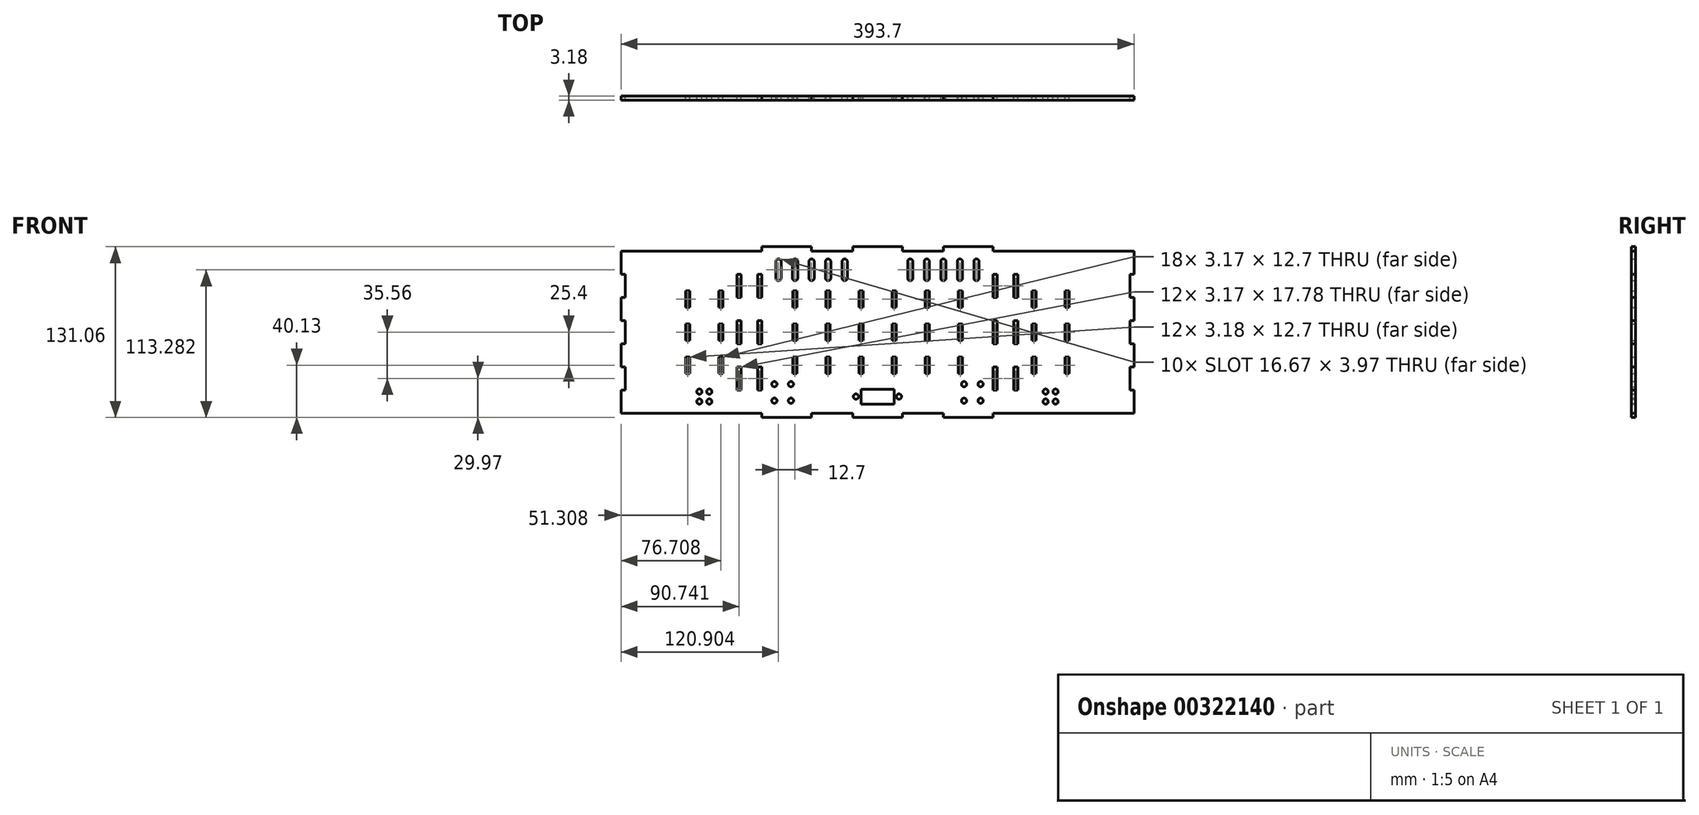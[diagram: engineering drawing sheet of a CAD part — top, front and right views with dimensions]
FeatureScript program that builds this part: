
annotation { "Feature Type Name" : "Feature", "Feature Type Description" : "" }
export const myFeature = defineFeature(function(context is Context, id is Id, definition is map)
    precondition{}
    {
        {
            var Q0;
            Q0=qCreatedBy(makeId("Front.planeOp"),FACE);
            var sketch = newSketch(context, id + "F0", { "sketchPlane" : qUnion([Q0])});
            skLineSegment(sketch, "E0.MirrorCS", {"start": v(-50.55, -65.53) * mm, "end": v(-50.55, -62.23) * mm});
            skLineSegment(sketch, "E1.MirrorCS", {"start": v(19.05, -65.53) * mm, "end": v(19.05, -62.23) * mm});
            skLineSegment(sketch, "E2.MirrorCS", {"start": v(50.55, -65.53) * mm, "end": v(50.55, -62.23) * mm});
            skLineSegment(sketch, "E3.MirrorCS", {"start": v(88.65, -65.53) * mm, "end": v(88.65, -62.23) * mm});
            skLineSegment(sketch, "E4.MirrorCS", {"start": v(-19.05, -65.53) * mm, "end": v(-19.05, -62.23) * mm});
            skLineSegment(sketch, "E5.MirrorCS", {"start": v(88.65, -65.53) * mm, "end": v(50.55, -65.53) * mm});
            skLineSegment(sketch, "E6.MirrorCS", {"start": v(-19.05, -65.53) * mm, "end": v(19.05, -65.53) * mm});
            skLineSegment(sketch, "E7.MirrorCS", {"start": v(-50.55, -65.53) * mm, "end": v(-19.05, -65.53) * mm, "construction": true});
            skLineSegment(sketch, "E8.MirrorCS", {"start": v(-88.65, -65.53) * mm, "end": v(-50.55, -65.53) * mm});
            skLineSegment(sketch, "E9.MirrorCS", {"start": v(-88.65, -65.53) * mm, "end": v(-88.65, -62.23) * mm});
            skLineSegment(sketch, "E10", {"start": v(-107.7, -62.23) * mm, "end": v(-88.65, -62.23) * mm});
            skLineSegment(sketch, "E11.trimOffspring", {"start": v(88.65, -62.23) * mm, "end": v(120.14, -62.23) * mm});
            skLineSegment(sketch, "E12.trimOffspring", {"start": v(19.05, -62.23) * mm, "end": v(50.55, -62.23) * mm});
            skLineSegment(sketch, "E13.trimOffspring", {"start": v(-50.55, -62.23) * mm, "end": v(-19.05, -62.23) * mm});
            skLineSegment(sketch, "E14", {"start": v(-107.7, 62.23) * mm, "end": v(-107.7, 44.45) * mm, "construction": true});
            skLineSegment(sketch, "E15.MirrorCS", {"start": v(-104.52, 26.67) * mm, "end": v(-104.52, 8.89) * mm, "construction": true});
            skLineSegment(sketch, "E16.MirrorCS", {"start": v(-107.7, -26.67) * mm, "end": v(-107.7, -8.89) * mm, "construction": true});
            skLineSegment(sketch, "E17.MirrorCS", {"start": v(-104.52, 44.45) * mm, "end": v(-104.52, 26.67) * mm});
            skLineSegment(sketch, "E18.MirrorCS", {"start": v(-104.52, -8.9) * mm, "end": v(-104.52, -26.67) * mm, "construction": true});
            skLineSegment(sketch, "E19.MirrorCS", {"start": v(-104.52, 26.67) * mm, "end": v(-107.7, 26.67) * mm});
            skLineSegment(sketch, "E20.MirrorCS", {"start": v(-107.7, 8.89) * mm, "end": v(-104.52, 8.89) * mm});
            skLineSegment(sketch, "E21.MirrorCS", {"start": v(-104.52, 8.89) * mm, "end": v(-104.52, -8.9) * mm});
            skLineSegment(sketch, "E22.MirrorCS", {"start": v(-104.52, -8.89) * mm, "end": v(-107.7, -8.89) * mm});
            skLineSegment(sketch, "E23.MirrorCS", {"start": v(-107.7, -26.67) * mm, "end": v(-104.52, -26.67) * mm});
            skLineSegment(sketch, "E24.MirrorCS", {"start": v(-107.7, 8.89) * mm, "end": v(-107.7, 26.67) * mm});
            skLineSegment(sketch, "E25.MirrorCS", {"start": v(-104.52, -26.67) * mm, "end": v(-104.52, -44.45) * mm});
            skLineSegment(sketch, "E26.MirrorCS", {"start": v(-104.52, -44.45) * mm, "end": v(-107.7, -44.45) * mm});
            skLineSegment(sketch, "E27.MirrorCS", {"start": v(-107.7, 44.45) * mm, "end": v(-104.52, 44.45) * mm});
            skLineSegment(sketch, "E28.trimOffspring", {"start": v(-107.7, 26.67) * mm, "end": v(-107.7, 8.89) * mm, "construction": true});
            skPoint(sketch, "E29.orphan", {"position": v(-107.7, 8.96) * mm});
            skLineSegment(sketch, "E30.trimOffspring", {"start": v(-107.7, -8.89) * mm, "end": v(-107.7, -26.67) * mm});
            skLineSegment(sketch, "E31.trimOffspring", {"start": v(-107.7, -44.45) * mm, "end": v(-107.7, -62.23) * mm, "construction": true});
            skPoint(sketch, "E32", {"position": v(-104.52, 0) * mm});
            skLineSegment(sketch, "E33.MirrorCS", {"start": v(-50.55, 65.53) * mm, "end": v(-19.05, 65.53) * mm, "construction": true});
            skLineSegment(sketch, "E34.MirrorCS", {"start": v(-88.65, 65.53) * mm, "end": v(-88.65, 62.23) * mm});
            skLineSegment(sketch, "E35.MirrorCS", {"start": v(88.65, 62.23) * mm, "end": v(120.14, 62.23) * mm});
            skLineSegment(sketch, "E36.MirrorCS", {"start": v(19.05, 65.53) * mm, "end": v(19.05, 62.23) * mm});
            skLineSegment(sketch, "E37.MirrorCS", {"start": v(88.65, 65.53) * mm, "end": v(88.65, 62.23) * mm});
            skLineSegment(sketch, "E38.MirrorCS", {"start": v(88.65, 65.53) * mm, "end": v(50.55, 65.53) * mm});
            skLineSegment(sketch, "E39.MirrorCS", {"start": v(-88.65, 65.53) * mm, "end": v(-50.55, 65.53) * mm});
            skLineSegment(sketch, "E40.MirrorCS", {"start": v(-107.7, 62.23) * mm, "end": v(-88.65, 62.23) * mm});
            skLineSegment(sketch, "E41.MirrorCS", {"start": v(19.05, 62.23) * mm, "end": v(50.55, 62.23) * mm});
            skLineSegment(sketch, "E42.MirrorCS", {"start": v(-50.55, 62.23) * mm, "end": v(-19.05, 62.23) * mm});
            skLineSegment(sketch, "E43.MirrorCS", {"start": v(-50.55, 65.53) * mm, "end": v(-50.55, 62.23) * mm});
            skLineSegment(sketch, "E44.MirrorCS", {"start": v(50.55, 65.53) * mm, "end": v(50.55, 62.23) * mm});
            skLineSegment(sketch, "E45.MirrorCS", {"start": v(-19.05, 65.53) * mm, "end": v(-19.05, 62.23) * mm});
            skLineSegment(sketch, "E46.MirrorCS", {"start": v(-19.05, 65.53) * mm, "end": v(19.05, 65.53) * mm});
            skPoint(sketch, "E47", {"position": v(0, 65.53) * mm});
            skLineSegment(sketch, "E48.MirrorCS", {"start": v(104.52, -44.45) * mm, "end": v(107.7, -44.45) * mm});
            skPoint(sketch, "E49.MirrorP", {"position": v(107.7, 8.96) * mm});
            skLineSegment(sketch, "E50.MirrorCS", {"start": v(104.52, 44.45) * mm, "end": v(104.52, 26.67) * mm});
            skLineSegment(sketch, "E51.MirrorCS", {"start": v(104.52, -8.89) * mm, "end": v(107.7, -8.89) * mm});
            skLineSegment(sketch, "E52.MirrorCS", {"start": v(107.7, -26.67) * mm, "end": v(104.52, -26.67) * mm});
            skLineSegment(sketch, "E53.MirrorCS", {"start": v(107.7, 26.67) * mm, "end": v(107.7, 8.89) * mm});
            skLineSegment(sketch, "E54.MirrorCS", {"start": v(107.7, -44.45) * mm, "end": v(107.7, -62.23) * mm, "construction": true});
            skLineSegment(sketch, "E55.MirrorCS", {"start": v(104.52, 26.67) * mm, "end": v(107.7, 26.67) * mm});
            skLineSegment(sketch, "E56.MirrorCS", {"start": v(104.52, -26.67) * mm, "end": v(104.52, -44.45) * mm});
            skLineSegment(sketch, "E57.MirrorCS", {"start": v(107.7, -26.67) * mm, "end": v(107.7, -8.89) * mm});
            skLineSegment(sketch, "E58.MirrorCS", {"start": v(104.52, 8.9) * mm, "end": v(104.52, -8.9) * mm});
            skLineSegment(sketch, "E59.MirrorCS", {"start": v(107.7, 62.23) * mm, "end": v(107.7, 44.45) * mm, "construction": true});
            skLineSegment(sketch, "E60.MirrorCS", {"start": v(107.7, 44.45) * mm, "end": v(104.52, 44.45) * mm});
            skLineSegment(sketch, "E61.MirrorCS", {"start": v(107.7, -8.89) * mm, "end": v(107.7, -26.67) * mm, "construction": true});
            skPoint(sketch, "E62.MirrorP", {"position": v(104.52, 0) * mm});
            skLineSegment(sketch, "E63.MirrorCS", {"start": v(104.52, -8.9) * mm, "end": v(104.52, -26.67) * mm, "construction": true});
            skLineSegment(sketch, "E64.MirrorCS", {"start": v(107.7, 8.89) * mm, "end": v(107.7, 26.67) * mm, "construction": true});
            skLineSegment(sketch, "E65.MirrorCS", {"start": v(104.52, 26.67) * mm, "end": v(104.52, 8.9) * mm, "construction": true});
            skLineSegment(sketch, "E66.MirrorCS", {"start": v(107.7, 8.89) * mm, "end": v(104.52, 8.89) * mm});
            skPoint(sketch, "E67.oppositeSnap0", {"position": v(-106.1, 26.67) * mm});
            skLineSegment(sketch, "E67.bottom", {"start": v(-91.82, 44.45) * mm, "end": v(-88.65, 44.45) * mm});
            skLineSegment(sketch, "E67.top", {"start": v(-91.82, 26.67) * mm, "end": v(-88.65, 26.67) * mm});
            skLineSegment(sketch, "E67.left", {"start": v(-91.82, 44.45) * mm, "end": v(-91.82, 26.67) * mm});
            skLineSegment(sketch, "E67.right", {"start": v(-88.65, 44.45) * mm, "end": v(-88.65, 26.67) * mm});
            skLineSegment(sketch, "E68.bottom", {"start": v(-91.82, 8.89) * mm, "end": v(-88.65, 8.89) * mm});
            skLineSegment(sketch, "E68.top", {"start": v(-91.82, -8.89) * mm, "end": v(-88.65, -8.89) * mm});
            skLineSegment(sketch, "E68.left", {"start": v(-91.82, 8.89) * mm, "end": v(-91.82, -8.89) * mm});
            skLineSegment(sketch, "E68.right", {"start": v(-88.65, 8.89) * mm, "end": v(-88.65, -8.89) * mm});
            skLineSegment(sketch, "E69.bottom", {"start": v(-88.65, -44.45) * mm, "end": v(-91.82, -44.45) * mm});
            skLineSegment(sketch, "E69.top", {"start": v(-88.65, -26.67) * mm, "end": v(-91.82, -26.67) * mm});
            skLineSegment(sketch, "E69.left", {"start": v(-88.65, -44.45) * mm, "end": v(-88.65, -26.67) * mm});
            skLineSegment(sketch, "E69.right", {"start": v(-91.82, -44.45) * mm, "end": v(-91.82, -26.67) * mm});
            skLineSegment(sketch, "E70.MirrorCS", {"start": v(91.82, 8.89) * mm, "end": v(88.65, 8.89) * mm});
            skLineSegment(sketch, "E71.MirrorCS", {"start": v(88.65, -26.67) * mm, "end": v(91.82, -26.67) * mm});
            skLineSegment(sketch, "E72.MirrorCS", {"start": v(91.82, 26.67) * mm, "end": v(88.65, 26.67) * mm});
            skLineSegment(sketch, "E73.MirrorCS", {"start": v(88.65, -44.45) * mm, "end": v(91.82, -44.45) * mm});
            skLineSegment(sketch, "E74.MirrorCS", {"start": v(91.82, 44.45) * mm, "end": v(88.65, 44.45) * mm});
            skLineSegment(sketch, "E75.MirrorCS", {"start": v(91.82, -8.89) * mm, "end": v(88.65, -8.89) * mm});
            skLineSegment(sketch, "E76.MirrorCS", {"start": v(91.82, -44.45) * mm, "end": v(91.82, -26.67) * mm});
            skLineSegment(sketch, "E77.MirrorCS", {"start": v(88.65, 44.45) * mm, "end": v(88.65, 26.67) * mm});
            skLineSegment(sketch, "E78.MirrorCS", {"start": v(88.65, -44.45) * mm, "end": v(88.65, -26.67) * mm});
            skLineSegment(sketch, "E79.MirrorCS", {"start": v(91.82, 44.45) * mm, "end": v(91.82, 26.67) * mm});
            skLineSegment(sketch, "E80.MirrorCS", {"start": v(88.65, 8.89) * mm, "end": v(88.65, -8.89) * mm});
            skLineSegment(sketch, "E81.MirrorCS", {"start": v(91.82, 8.89) * mm, "end": v(91.82, -8.89) * mm});
            skLineSegment(sketch, "E82.bottom", {"start": v(-65.09, -19.05) * mm, "end": v(-61.91, -19.05) * mm});
            skLineSegment(sketch, "E82.top", {"start": v(-65.09, -31.75) * mm, "end": v(-61.91, -31.75) * mm});
            skLineSegment(sketch, "E82.left", {"start": v(-65.09, -19.05) * mm, "end": v(-65.09, -31.75) * mm});
            skLineSegment(sketch, "E82.right", {"start": v(-61.91, -19.05) * mm, "end": v(-61.91, -31.75) * mm});
            skLineSegment(sketch, "E83.0.1.0", {"start": v(-65.09, 6.35) * mm, "end": v(-61.91, 6.35) * mm});
            skLineSegment(sketch, "E83.0.1.1", {"start": v(-65.09, -6.35) * mm, "end": v(-61.91, -6.35) * mm});
            skLineSegment(sketch, "E83.0.1.2", {"start": v(-65.09, 6.35) * mm, "end": v(-65.09, -6.35) * mm});
            skLineSegment(sketch, "E83.0.1.3", {"start": v(-61.91, 6.35) * mm, "end": v(-61.91, -6.35) * mm});
            skLineSegment(sketch, "E83.0.2.0", {"start": v(-65.09, 31.75) * mm, "end": v(-61.91, 31.75) * mm});
            skLineSegment(sketch, "E83.0.2.1", {"start": v(-65.09, 19.05) * mm, "end": v(-61.91, 19.05) * mm});
            skLineSegment(sketch, "E83.0.2.2", {"start": v(-65.09, 31.75) * mm, "end": v(-65.09, 19.05) * mm});
            skLineSegment(sketch, "E83.0.2.3", {"start": v(-61.91, 31.75) * mm, "end": v(-61.91, 19.05) * mm});
            skLineSegment(sketch, "E83.1.0.0", {"start": v(-39.69, -19.05) * mm, "end": v(-36.51, -19.05) * mm});
            skLineSegment(sketch, "E83.1.0.1", {"start": v(-39.69, -31.75) * mm, "end": v(-36.51, -31.75) * mm});
            skLineSegment(sketch, "E83.1.0.2", {"start": v(-39.69, -19.05) * mm, "end": v(-39.69, -31.75) * mm});
            skLineSegment(sketch, "E83.1.0.3", {"start": v(-36.51, -19.05) * mm, "end": v(-36.51, -31.75) * mm});
            skLineSegment(sketch, "E83.1.1.0", {"start": v(-39.69, 6.35) * mm, "end": v(-36.51, 6.35) * mm});
            skLineSegment(sketch, "E83.1.1.1", {"start": v(-39.69, -6.35) * mm, "end": v(-36.51, -6.35) * mm});
            skLineSegment(sketch, "E83.1.1.2", {"start": v(-39.69, 6.35) * mm, "end": v(-39.69, -6.35) * mm});
            skLineSegment(sketch, "E83.1.1.3", {"start": v(-36.51, 6.35) * mm, "end": v(-36.51, -6.35) * mm});
            skLineSegment(sketch, "E83.1.2.0", {"start": v(-39.69, 31.75) * mm, "end": v(-36.51, 31.75) * mm});
            skLineSegment(sketch, "E83.1.2.1", {"start": v(-39.69, 19.05) * mm, "end": v(-36.51, 19.05) * mm});
            skLineSegment(sketch, "E83.1.2.2", {"start": v(-39.69, 31.75) * mm, "end": v(-39.69, 19.05) * mm});
            skLineSegment(sketch, "E83.1.2.3", {"start": v(-36.51, 31.75) * mm, "end": v(-36.51, 19.05) * mm});
            skLineSegment(sketch, "E83.2.0.0", {"start": v(-14.29, -19.05) * mm, "end": v(-11.11, -19.05) * mm});
            skLineSegment(sketch, "E83.2.0.1", {"start": v(-14.29, -31.75) * mm, "end": v(-11.11, -31.75) * mm});
            skLineSegment(sketch, "E83.2.0.2", {"start": v(-14.29, -19.05) * mm, "end": v(-14.29, -31.75) * mm});
            skLineSegment(sketch, "E83.2.0.3", {"start": v(-11.11, -19.05) * mm, "end": v(-11.11, -31.75) * mm});
            skLineSegment(sketch, "E83.2.1.0", {"start": v(-14.29, 6.35) * mm, "end": v(-11.11, 6.35) * mm});
            skLineSegment(sketch, "E83.2.1.1", {"start": v(-14.29, -6.35) * mm, "end": v(-11.11, -6.35) * mm});
            skLineSegment(sketch, "E83.2.1.2", {"start": v(-14.29, 6.35) * mm, "end": v(-14.29, -6.35) * mm});
            skLineSegment(sketch, "E83.2.1.3", {"start": v(-11.11, 6.35) * mm, "end": v(-11.11, -6.35) * mm});
            skLineSegment(sketch, "E83.2.2.0", {"start": v(-14.29, 31.75) * mm, "end": v(-11.11, 31.75) * mm});
            skLineSegment(sketch, "E83.2.2.1", {"start": v(-14.29, 19.05) * mm, "end": v(-11.11, 19.05) * mm});
            skLineSegment(sketch, "E83.2.2.2", {"start": v(-14.29, 31.75) * mm, "end": v(-14.29, 19.05) * mm});
            skLineSegment(sketch, "E83.2.2.3", {"start": v(-11.11, 31.75) * mm, "end": v(-11.11, 19.05) * mm});
            skLineSegment(sketch, "E83.3.0.0", {"start": v(11.11, -19.05) * mm, "end": v(14.29, -19.05) * mm});
            skLineSegment(sketch, "E83.3.0.1", {"start": v(11.11, -31.75) * mm, "end": v(14.29, -31.75) * mm});
            skLineSegment(sketch, "E83.3.0.2", {"start": v(11.11, -19.05) * mm, "end": v(11.11, -31.75) * mm});
            skLineSegment(sketch, "E83.3.0.3", {"start": v(14.29, -19.05) * mm, "end": v(14.29, -31.75) * mm});
            skLineSegment(sketch, "E83.3.1.0", {"start": v(11.11, 6.35) * mm, "end": v(14.29, 6.35) * mm});
            skLineSegment(sketch, "E83.3.1.1", {"start": v(11.11, -6.35) * mm, "end": v(14.29, -6.35) * mm});
            skLineSegment(sketch, "E83.3.1.2", {"start": v(11.11, 6.35) * mm, "end": v(11.11, -6.35) * mm});
            skLineSegment(sketch, "E83.3.1.3", {"start": v(14.29, 6.35) * mm, "end": v(14.29, -6.35) * mm});
            skLineSegment(sketch, "E83.3.2.0", {"start": v(11.11, 31.75) * mm, "end": v(14.29, 31.75) * mm});
            skLineSegment(sketch, "E83.3.2.1", {"start": v(11.11, 19.05) * mm, "end": v(14.29, 19.05) * mm});
            skLineSegment(sketch, "E83.3.2.2", {"start": v(11.11, 31.75) * mm, "end": v(11.11, 19.05) * mm});
            skLineSegment(sketch, "E83.3.2.3", {"start": v(14.29, 31.75) * mm, "end": v(14.29, 19.05) * mm});
            skLineSegment(sketch, "E83.4.0.0", {"start": v(36.51, -19.05) * mm, "end": v(39.69, -19.05) * mm});
            skLineSegment(sketch, "E83.4.0.1", {"start": v(36.51, -31.75) * mm, "end": v(39.69, -31.75) * mm});
            skLineSegment(sketch, "E83.4.0.2", {"start": v(36.51, -19.05) * mm, "end": v(36.51, -31.75) * mm});
            skLineSegment(sketch, "E83.4.0.3", {"start": v(39.69, -19.05) * mm, "end": v(39.69, -31.75) * mm});
            skLineSegment(sketch, "E83.4.1.0", {"start": v(36.51, 6.35) * mm, "end": v(39.69, 6.35) * mm});
            skLineSegment(sketch, "E83.4.1.1", {"start": v(36.51, -6.35) * mm, "end": v(39.69, -6.35) * mm});
            skLineSegment(sketch, "E83.4.1.2", {"start": v(36.51, 6.35) * mm, "end": v(36.51, -6.35) * mm});
            skLineSegment(sketch, "E83.4.1.3", {"start": v(39.69, 6.35) * mm, "end": v(39.69, -6.35) * mm});
            skLineSegment(sketch, "E83.4.2.0", {"start": v(36.51, 31.75) * mm, "end": v(39.69, 31.75) * mm});
            skLineSegment(sketch, "E83.4.2.1", {"start": v(36.51, 19.05) * mm, "end": v(39.69, 19.05) * mm});
            skLineSegment(sketch, "E83.4.2.2", {"start": v(36.51, 31.75) * mm, "end": v(36.51, 19.05) * mm});
            skLineSegment(sketch, "E83.4.2.3", {"start": v(39.69, 31.75) * mm, "end": v(39.69, 19.05) * mm});
            skLineSegment(sketch, "E83.5.0.0", {"start": v(61.91, -19.05) * mm, "end": v(65.09, -19.05) * mm});
            skLineSegment(sketch, "E83.5.0.1", {"start": v(61.91, -31.75) * mm, "end": v(65.09, -31.75) * mm});
            skLineSegment(sketch, "E83.5.0.2", {"start": v(61.91, -19.05) * mm, "end": v(61.91, -31.75) * mm});
            skLineSegment(sketch, "E83.5.0.3", {"start": v(65.09, -19.05) * mm, "end": v(65.09, -31.75) * mm});
            skLineSegment(sketch, "E83.5.1.0", {"start": v(61.91, 6.35) * mm, "end": v(65.09, 6.35) * mm});
            skLineSegment(sketch, "E83.5.1.1", {"start": v(61.91, -6.35) * mm, "end": v(65.09, -6.35) * mm});
            skLineSegment(sketch, "E83.5.1.2", {"start": v(61.91, 6.35) * mm, "end": v(61.91, -6.35) * mm});
            skLineSegment(sketch, "E83.5.1.3", {"start": v(65.09, 6.35) * mm, "end": v(65.09, -6.35) * mm});
            skLineSegment(sketch, "E83.5.2.0", {"start": v(61.91, 31.75) * mm, "end": v(65.09, 31.75) * mm});
            skLineSegment(sketch, "E83.5.2.1", {"start": v(61.91, 19.05) * mm, "end": v(65.09, 19.05) * mm});
            skLineSegment(sketch, "E83.5.2.2", {"start": v(61.91, 31.75) * mm, "end": v(61.91, 19.05) * mm});
            skLineSegment(sketch, "E83.5.2.3", {"start": v(65.09, 31.75) * mm, "end": v(65.09, 19.05) * mm});
            skLineSegment(sketch, "E83.direction1", {"start": v(-65.09, -31.75) * mm, "end": v(-39.69, -31.75) * mm, "construction": true});
            skLineSegment(sketch, "E83.direction2", {"start": v(-65.09, -31.75) * mm, "end": v(-65.09, -6.35) * mm, "construction": true});
            skLineSegment(sketch, "E84", {"start": v(11.11, -25.4) * mm, "end": v(-11.11, -25.4) * mm, "construction": true});
            skPoint(sketch, "E85", {"position": v(0, -25.4) * mm});
            skLineSegment(sketch, "E86", {"start": v(-75.95, 54.1) * mm, "end": v(-25.15, 54.1) * mm, "construction": true});
            skArc(sketch, "E87", {"start": v(-23.16, 54.1) * mm, "mid": v(-25.15, 56.09) * mm, "end": v(-27.13, 54.1) * mm});
            skArc(sketch, "E88", {"start": v(-27.13, 41.4) * mm, "mid": v(-25.15, 39.42) * mm, "end": v(-23.16, 41.4) * mm});
            skLineSegment(sketch, "E89", {"start": v(-23.16, 54.1) * mm, "end": v(-23.16, 41.4) * mm});
            skLineSegment(sketch, "E90", {"start": v(-27.13, 54.1) * mm, "end": v(-27.13, 41.4) * mm});
            skArc(sketch, "E91.1.0.0", {"start": v(-35.86, 54.1) * mm, "mid": v(-37.85, 56.09) * mm, "end": v(-39.83, 54.1) * mm});
            skLineSegment(sketch, "E91.1.0.1", {"start": v(-35.86, 54.1) * mm, "end": v(-35.86, 41.4) * mm});
            skArc(sketch, "E91.1.0.2", {"start": v(-39.83, 41.4) * mm, "mid": v(-37.85, 39.42) * mm, "end": v(-35.86, 41.4) * mm});
            skLineSegment(sketch, "E91.1.0.3", {"start": v(-39.83, 54.1) * mm, "end": v(-39.83, 41.4) * mm});
            skArc(sketch, "E91.2.0.0", {"start": v(-48.56, 54.1) * mm, "mid": v(-50.55, 56.09) * mm, "end": v(-52.53, 54.1) * mm});
            skLineSegment(sketch, "E91.2.0.1", {"start": v(-48.56, 54.1) * mm, "end": v(-48.56, 41.4) * mm});
            skArc(sketch, "E91.2.0.2", {"start": v(-52.53, 41.4) * mm, "mid": v(-50.55, 39.42) * mm, "end": v(-48.56, 41.4) * mm});
            skLineSegment(sketch, "E91.2.0.3", {"start": v(-52.53, 54.1) * mm, "end": v(-52.53, 41.4) * mm});
            skArc(sketch, "E91.3.0.0", {"start": v(-61.26, 54.1) * mm, "mid": v(-63.25, 56.09) * mm, "end": v(-65.23, 54.1) * mm});
            skLineSegment(sketch, "E91.3.0.1", {"start": v(-61.26, 54.1) * mm, "end": v(-61.26, 41.4) * mm});
            skArc(sketch, "E91.3.0.2", {"start": v(-65.23, 41.4) * mm, "mid": v(-63.25, 39.42) * mm, "end": v(-61.26, 41.4) * mm});
            skLineSegment(sketch, "E91.3.0.3", {"start": v(-65.23, 54.1) * mm, "end": v(-65.23, 41.4) * mm});
            skArc(sketch, "E91.4.0.0", {"start": v(-73.96, 54.1) * mm, "mid": v(-75.95, 56.09) * mm, "end": v(-77.93, 54.1) * mm});
            skLineSegment(sketch, "E91.4.0.1", {"start": v(-73.96, 54.1) * mm, "end": v(-73.96, 41.4) * mm});
            skArc(sketch, "E91.4.0.2", {"start": v(-77.93, 41.4) * mm, "mid": v(-75.95, 39.42) * mm, "end": v(-73.96, 41.4) * mm});
            skLineSegment(sketch, "E91.4.0.3", {"start": v(-77.93, 54.1) * mm, "end": v(-77.93, 41.4) * mm});
            skLineSegment(sketch, "E91.direction1", {"start": v(-27.13, 41.4) * mm, "end": v(-39.83, 41.4) * mm, "construction": true});
            skArc(sketch, "E92.MirrorCS", {"start": v(39.83, 41.4) * mm, "mid": v(37.85, 39.42) * mm, "end": v(35.86, 41.4) * mm});
            skArc(sketch, "E93.MirrorCS", {"start": v(73.96, 54.1) * mm, "mid": v(75.95, 56.09) * mm, "end": v(77.93, 54.1) * mm});
            skLineSegment(sketch, "E94.MirrorCS", {"start": v(61.26, 54.1) * mm, "end": v(61.26, 41.4) * mm});
            skLineSegment(sketch, "E95.MirrorCS", {"start": v(23.16, 54.1) * mm, "end": v(23.16, 41.4) * mm});
            skArc(sketch, "E96.MirrorCS", {"start": v(48.56, 54.1) * mm, "mid": v(50.55, 56.09) * mm, "end": v(52.53, 54.1) * mm});
            skArc(sketch, "E97.MirrorCS", {"start": v(77.93, 41.4) * mm, "mid": v(75.95, 39.42) * mm, "end": v(73.96, 41.4) * mm});
            skLineSegment(sketch, "E98.MirrorCS", {"start": v(75.95, 54.1) * mm, "end": v(25.15, 54.1) * mm, "construction": true});
            skArc(sketch, "E99.MirrorCS", {"start": v(35.86, 54.1) * mm, "mid": v(37.85, 56.09) * mm, "end": v(39.83, 54.1) * mm});
            skLineSegment(sketch, "E100.MirrorCS", {"start": v(35.86, 54.1) * mm, "end": v(35.86, 41.4) * mm});
            skArc(sketch, "E101.MirrorCS", {"start": v(52.53, 41.4) * mm, "mid": v(50.55, 39.42) * mm, "end": v(48.56, 41.4) * mm});
            skLineSegment(sketch, "E102.MirrorCS", {"start": v(65.23, 54.1) * mm, "end": v(65.23, 41.4) * mm});
            skLineSegment(sketch, "E103.MirrorCS", {"start": v(27.13, 41.4) * mm, "end": v(39.83, 41.4) * mm, "construction": true});
            skArc(sketch, "E104.MirrorCS", {"start": v(61.26, 54.1) * mm, "mid": v(63.25, 56.09) * mm, "end": v(65.23, 54.1) * mm});
            skArc(sketch, "E105.MirrorCS", {"start": v(27.13, 41.4) * mm, "mid": v(25.15, 39.42) * mm, "end": v(23.16, 41.4) * mm});
            skLineSegment(sketch, "E106.MirrorCS", {"start": v(39.83, 54.1) * mm, "end": v(39.83, 41.4) * mm});
            skLineSegment(sketch, "E107.MirrorCS", {"start": v(73.96, 54.1) * mm, "end": v(73.96, 41.4) * mm});
            skLineSegment(sketch, "E108.MirrorCS", {"start": v(27.13, 54.1) * mm, "end": v(27.13, 41.4) * mm});
            skLineSegment(sketch, "E109.MirrorCS", {"start": v(48.56, 54.1) * mm, "end": v(48.56, 41.4) * mm});
            skArc(sketch, "E110.MirrorCS", {"start": v(65.23, 41.4) * mm, "mid": v(63.25, 39.42) * mm, "end": v(61.26, 41.4) * mm});
            skLineSegment(sketch, "E111.MirrorCS", {"start": v(77.93, 54.1) * mm, "end": v(77.93, 41.4) * mm});
            skLineSegment(sketch, "E112.MirrorCS", {"start": v(52.53, 54.1) * mm, "end": v(52.53, 41.4) * mm});
            skArc(sketch, "E113.MirrorCS", {"start": v(23.16, 54.1) * mm, "mid": v(25.15, 56.09) * mm, "end": v(27.13, 54.1) * mm});
            skLineSegment(sketch, "E114", {"start": v(-88.65, -44.45) * mm, "end": v(-88.65, -62.23) * mm, "construction": true});
            skCircle(sketch, "E115", {"center": v(-79.12, -52.7) * mm, "radius": 1.98 * mm});
            skCircle(sketch, "E116", {"center": v(-66.42, -52.7) * mm, "radius": 1.98 * mm});
            skCircle(sketch, "E117", {"center": v(-66.42, -40) * mm, "radius": 1.98 * mm});
            skCircle(sketch, "E118", {"center": v(-79.12, -40) * mm, "radius": 1.98 * mm});
            skCircle(sketch, "E119.MirrorC", {"center": v(79.12, -40) * mm, "radius": 1.98 * mm});
            skCircle(sketch, "E120.MirrorC", {"center": v(79.12, -52.7) * mm, "radius": 1.98 * mm});
            skCircle(sketch, "E121.MirrorC", {"center": v(66.42, -40) * mm, "radius": 1.98 * mm});
            skCircle(sketch, "E122.MirrorC", {"center": v(66.42, -52.7) * mm, "radius": 1.98 * mm});
            skPoint(sketch, "E123.1.0.0", {"position": v(-193.68, 0) * mm});
            skLineSegment(sketch, "E123.1.0.1", {"start": v(-196.85, -44.45) * mm, "end": v(-196.85, -62.23) * mm});
            skLineSegment(sketch, "E123.1.0.2", {"start": v(-196.85, -26.67) * mm, "end": v(-196.85, -8.89) * mm});
            skLineSegment(sketch, "E123.1.0.3", {"start": v(-193.68, 44.45) * mm, "end": v(-193.68, 26.67) * mm});
            skPoint(sketch, "E123.1.0.4", {"position": v(-195.26, 26.67) * mm});
            skLineSegment(sketch, "E123.1.0.5", {"start": v(-193.68, -8.89) * mm, "end": v(-193.68, -26.67) * mm, "construction": true});
            skLineSegment(sketch, "E123.1.0.6", {"start": v(-193.68, -26.67) * mm, "end": v(-193.68, -44.45) * mm});
            skLineSegment(sketch, "E123.1.0.7", {"start": v(-196.85, 26.67) * mm, "end": v(-196.85, 8.89) * mm});
            skPoint(sketch, "E123.1.0.8", {"position": v(-196.85, 8.96) * mm});
            skLineSegment(sketch, "E123.1.0.9", {"start": v(-196.85, 62.23) * mm, "end": v(-196.85, 44.45) * mm});
            skLineSegment(sketch, "E123.1.0.10", {"start": v(-193.68, 26.67) * mm, "end": v(-193.68, 8.89) * mm, "construction": true});
            skLineSegment(sketch, "E123.1.0.11", {"start": v(-196.85, -8.89) * mm, "end": v(-196.85, -26.67) * mm});
            skLineSegment(sketch, "E123.1.0.12", {"start": v(-193.68, 8.89) * mm, "end": v(-193.68, -8.89) * mm});
            skLineSegment(sketch, "E123.1.0.13", {"start": v(-196.85, 8.89) * mm, "end": v(-196.85, 26.67) * mm});
            skLineSegment(sketch, "E123.1.0.14", {"start": v(-193.68, -44.45) * mm, "end": v(-196.85, -44.45) * mm});
            skLineSegment(sketch, "E123.1.0.15", {"start": v(-196.85, 44.45) * mm, "end": v(-193.68, 44.45) * mm});
            skLineSegment(sketch, "E123.1.0.16", {"start": v(-193.68, -8.89) * mm, "end": v(-196.85, -8.89) * mm});
            skLineSegment(sketch, "E123.1.0.17", {"start": v(-196.85, -26.67) * mm, "end": v(-193.68, -26.67) * mm});
            skLineSegment(sketch, "E123.1.0.18", {"start": v(-193.68, 26.67) * mm, "end": v(-196.85, 26.67) * mm});
            skLineSegment(sketch, "E123.1.0.19", {"start": v(-196.85, 8.89) * mm, "end": v(-193.68, 8.89) * mm});
            skLineSegment(sketch, "E123.direction1", {"start": v(-107.7, -62.23) * mm, "end": v(-196.85, -62.23) * mm, "construction": true});
            skLineSegment(sketch, "E124", {"start": v(-107.7, 62.23) * mm, "end": v(-196.85, 62.23) * mm});
            skLineSegment(sketch, "E125", {"start": v(-107.7, -62.23) * mm, "end": v(-196.85, -62.23) * mm});
            skLineSegment(sketch, "E126.MirrorCS", {"start": v(193.68, 26.67) * mm, "end": v(196.85, 26.67) * mm});
            skLineSegment(sketch, "E127.MirrorCS", {"start": v(196.85, 8.89) * mm, "end": v(193.68, 8.89) * mm});
            skLineSegment(sketch, "E128.MirrorCS", {"start": v(193.68, -8.89) * mm, "end": v(196.85, -8.89) * mm});
            skLineSegment(sketch, "E129.MirrorCS", {"start": v(196.85, -26.67) * mm, "end": v(193.68, -26.67) * mm});
            skLineSegment(sketch, "E130.MirrorCS", {"start": v(193.68, -44.45) * mm, "end": v(196.85, -44.45) * mm});
            skLineSegment(sketch, "E131.MirrorCS", {"start": v(196.85, 44.45) * mm, "end": v(193.68, 44.45) * mm});
            skLineSegment(sketch, "E132.MirrorCS", {"start": v(196.85, 26.67) * mm, "end": v(196.85, 8.89) * mm});
            skLineSegment(sketch, "E133.MirrorCS", {"start": v(193.68, 8.89) * mm, "end": v(193.68, -8.89) * mm});
            skLineSegment(sketch, "E134.MirrorCS", {"start": v(196.85, -26.67) * mm, "end": v(196.85, -8.89) * mm});
            skLineSegment(sketch, "E135.MirrorCS", {"start": v(107.7, -62.23) * mm, "end": v(196.85, -62.23) * mm});
            skPoint(sketch, "E136.MirrorP", {"position": v(195.26, 26.67) * mm});
            skPoint(sketch, "E137.MirrorP", {"position": v(196.85, 8.96) * mm});
            skLineSegment(sketch, "E138.MirrorCS", {"start": v(193.68, -8.89) * mm, "end": v(193.68, -26.67) * mm, "construction": true});
            skLineSegment(sketch, "E139.MirrorCS", {"start": v(193.68, -26.67) * mm, "end": v(193.68, -44.45) * mm});
            skLineSegment(sketch, "E140.MirrorCS", {"start": v(107.7, -62.23) * mm, "end": v(196.85, -62.23) * mm, "construction": true});
            skLineSegment(sketch, "E141.MirrorCS", {"start": v(193.68, 26.67) * mm, "end": v(193.68, 8.89) * mm, "construction": true});
            skLineSegment(sketch, "E142.MirrorCS", {"start": v(196.85, 62.23) * mm, "end": v(196.85, 44.45) * mm});
            skLineSegment(sketch, "E143.MirrorCS", {"start": v(196.85, -8.89) * mm, "end": v(196.85, -26.67) * mm});
            skLineSegment(sketch, "E144.MirrorCS", {"start": v(196.85, -44.45) * mm, "end": v(196.85, -62.23) * mm});
            skPoint(sketch, "E145.MirrorP", {"position": v(193.68, 0) * mm});
            skLineSegment(sketch, "E146.MirrorCS", {"start": v(107.7, 62.23) * mm, "end": v(196.85, 62.23) * mm});
            skLineSegment(sketch, "E147.MirrorCS", {"start": v(193.68, 44.45) * mm, "end": v(193.68, 26.67) * mm});
            skLineSegment(sketch, "E148.MirrorCS", {"start": v(196.85, 8.89) * mm, "end": v(196.85, 26.67) * mm});
            skLineSegment(sketch, "E149", {"start": v(-107.7, 44.45) * mm, "end": v(-107.7, -44.45) * mm});
            skLineSegment(sketch, "E150", {"start": v(107.7, 44.45) * mm, "end": v(107.7, -44.45) * mm});
            skLineSegment(sketch, "E151.MirrorCS", {"start": v(-118.55, -31.75) * mm, "end": v(-121.73, -31.75) * mm});
            skLineSegment(sketch, "E152.MirrorCS", {"start": v(-118.55, -6.35) * mm, "end": v(-121.73, -6.35) * mm});
            skLineSegment(sketch, "E153.MirrorCS", {"start": v(-143.95, -31.75) * mm, "end": v(-147.13, -31.75) * mm});
            skLineSegment(sketch, "E154.MirrorCS", {"start": v(-118.55, 6.35) * mm, "end": v(-121.73, 6.35) * mm});
            skLineSegment(sketch, "E155.MirrorCS", {"start": v(-143.95, 31.75) * mm, "end": v(-147.13, 31.75) * mm});
            skLineSegment(sketch, "E156.MirrorCS", {"start": v(-143.95, 19.05) * mm, "end": v(-147.13, 19.05) * mm});
            skLineSegment(sketch, "E157.MirrorCS", {"start": v(-118.55, -19.05) * mm, "end": v(-121.73, -19.05) * mm});
            skLineSegment(sketch, "E158.MirrorCS", {"start": v(-143.95, -6.35) * mm, "end": v(-147.13, -6.35) * mm});
            skLineSegment(sketch, "E159.MirrorCS", {"start": v(-143.95, 6.35) * mm, "end": v(-147.13, 6.35) * mm});
            skLineSegment(sketch, "E160.MirrorCS", {"start": v(-143.95, -19.05) * mm, "end": v(-147.13, -19.05) * mm});
            skLineSegment(sketch, "E161.MirrorCS", {"start": v(-118.55, 19.05) * mm, "end": v(-121.73, 19.05) * mm});
            skLineSegment(sketch, "E162.MirrorCS", {"start": v(-118.55, 31.75) * mm, "end": v(-121.73, 31.75) * mm});
            skLineSegment(sketch, "E163.MirrorCS", {"start": v(-118.55, -19.05) * mm, "end": v(-118.55, -31.75) * mm});
            skLineSegment(sketch, "E164.MirrorCS", {"start": v(-121.73, -19.05) * mm, "end": v(-121.73, -31.75) * mm});
            skLineSegment(sketch, "E165.MirrorCS", {"start": v(-147.13, 6.35) * mm, "end": v(-147.13, -6.35) * mm});
            skLineSegment(sketch, "E166.MirrorCS", {"start": v(-143.95, -19.05) * mm, "end": v(-143.95, -31.75) * mm});
            skLineSegment(sketch, "E167.MirrorCS", {"start": v(-118.55, 31.75) * mm, "end": v(-118.55, 19.05) * mm});
            skLineSegment(sketch, "E168.MirrorCS", {"start": v(-147.13, 31.75) * mm, "end": v(-147.13, 19.05) * mm});
            skLineSegment(sketch, "E169.MirrorCS", {"start": v(-147.13, -19.05) * mm, "end": v(-147.13, -31.75) * mm});
            skLineSegment(sketch, "E170.MirrorCS", {"start": v(-143.95, 6.35) * mm, "end": v(-143.95, -6.35) * mm});
            skLineSegment(sketch, "E171.MirrorCS", {"start": v(-121.73, 31.75) * mm, "end": v(-121.73, 19.05) * mm});
            skLineSegment(sketch, "E172.MirrorCS", {"start": v(-118.55, -31.75) * mm, "end": v(-118.55, -6.35) * mm, "construction": true});
            skLineSegment(sketch, "E173.MirrorCS", {"start": v(-118.55, -31.75) * mm, "end": v(-143.95, -31.75) * mm, "construction": true});
            skLineSegment(sketch, "E174.MirrorCS", {"start": v(-143.95, 31.75) * mm, "end": v(-143.95, 19.05) * mm});
            skLineSegment(sketch, "E175.MirrorCS", {"start": v(-118.55, 6.35) * mm, "end": v(-118.55, -6.35) * mm});
            skLineSegment(sketch, "E176.MirrorCS", {"start": v(-121.73, 6.35) * mm, "end": v(-121.73, -6.35) * mm});
            skLineSegment(sketch, "E177.MirrorCS", {"start": v(147.13, 19.05) * mm, "end": v(143.95, 19.05) * mm});
            skLineSegment(sketch, "E178.MirrorCS", {"start": v(121.73, -6.35) * mm, "end": v(118.55, -6.35) * mm});
            skLineSegment(sketch, "E179.MirrorCS", {"start": v(147.13, -6.35) * mm, "end": v(143.95, -6.35) * mm});
            skLineSegment(sketch, "E180.MirrorCS", {"start": v(121.73, -31.75) * mm, "end": v(118.55, -31.75) * mm});
            skLineSegment(sketch, "E181.MirrorCS", {"start": v(121.73, 6.35) * mm, "end": v(118.55, 6.35) * mm});
            skLineSegment(sketch, "E182.MirrorCS", {"start": v(147.13, -19.05) * mm, "end": v(143.95, -19.05) * mm});
            skLineSegment(sketch, "E183.MirrorCS", {"start": v(121.73, 31.75) * mm, "end": v(118.55, 31.75) * mm});
            skLineSegment(sketch, "E184.MirrorCS", {"start": v(147.13, 6.35) * mm, "end": v(143.95, 6.35) * mm});
            skLineSegment(sketch, "E185.MirrorCS", {"start": v(121.73, 19.05) * mm, "end": v(118.55, 19.05) * mm});
            skLineSegment(sketch, "E186.MirrorCS", {"start": v(147.13, 31.75) * mm, "end": v(143.95, 31.75) * mm});
            skLineSegment(sketch, "E187.MirrorCS", {"start": v(121.73, -19.05) * mm, "end": v(118.55, -19.05) * mm});
            skLineSegment(sketch, "E188.MirrorCS", {"start": v(147.13, -31.75) * mm, "end": v(143.95, -31.75) * mm});
            skLineSegment(sketch, "E189.MirrorCS", {"start": v(147.13, 31.75) * mm, "end": v(147.13, 19.05) * mm});
            skLineSegment(sketch, "E190.MirrorCS", {"start": v(143.95, 31.75) * mm, "end": v(143.95, 19.05) * mm});
            skLineSegment(sketch, "E191.MirrorCS", {"start": v(121.73, -19.05) * mm, "end": v(121.73, -31.75) * mm});
            skLineSegment(sketch, "E192.MirrorCS", {"start": v(118.55, -19.05) * mm, "end": v(118.55, -31.75) * mm});
            skLineSegment(sketch, "E193.MirrorCS", {"start": v(147.13, 6.35) * mm, "end": v(147.13, -6.35) * mm});
            skLineSegment(sketch, "E194.MirrorCS", {"start": v(118.55, 6.35) * mm, "end": v(118.55, -6.35) * mm});
            skLineSegment(sketch, "E195.MirrorCS", {"start": v(143.95, -19.05) * mm, "end": v(143.95, -31.75) * mm});
            skLineSegment(sketch, "E196.MirrorCS", {"start": v(143.95, 6.35) * mm, "end": v(143.95, -6.35) * mm});
            skLineSegment(sketch, "E197.MirrorCS", {"start": v(118.55, 31.75) * mm, "end": v(118.55, 19.05) * mm});
            skLineSegment(sketch, "E198.MirrorCS", {"start": v(121.73, 31.75) * mm, "end": v(121.73, 19.05) * mm});
            skLineSegment(sketch, "E199.MirrorCS", {"start": v(147.13, -19.05) * mm, "end": v(147.13, -31.75) * mm});
            skLineSegment(sketch, "E200.MirrorCS", {"start": v(121.73, 6.35) * mm, "end": v(121.73, -6.35) * mm});
            skLineSegment(sketch, "E201.bottom", {"start": v(12.7, -55.25) * mm, "end": v(-12.7, -55.25) * mm});
            skLineSegment(sketch, "E201.top", {"start": v(12.7, -43.81) * mm, "end": v(-12.7, -43.81) * mm});
            skLineSegment(sketch, "E201.left", {"start": v(12.7, -55.25) * mm, "end": v(12.7, -43.81) * mm});
            skLineSegment(sketch, "E201.right", {"start": v(-12.7, -55.25) * mm, "end": v(-12.7, -43.81) * mm});
            skPoint(sketch, "E201.middle", {"position": v(0, -49.53) * mm});
            skCircle(sketch, "E202", {"center": v(-16.51, -49.53) * mm, "radius": 1.98 * mm});
            skPoint(sketch, "E202.centerSnap0", {"position": v(-12.7, -49.53) * mm});
            skCircle(sketch, "E203", {"center": v(16.5, -49.53) * mm, "radius": 1.98 * mm});
            skPoint(sketch, "E203.centerSnap0", {"position": v(12.7, -49.53) * mm});
            skCircle(sketch, "E204", {"center": v(-136.65, -45.72) * mm, "radius": 1.98 * mm});
            skCircle(sketch, "E205.0.1.0", {"center": v(-136.65, -53.34) * mm, "radius": 1.98 * mm});
            skCircle(sketch, "E205.1.0.0", {"center": v(-129.03, -45.72) * mm, "radius": 1.98 * mm});
            skCircle(sketch, "E205.1.1.0", {"center": v(-129.03, -53.34) * mm, "radius": 1.98 * mm});
            skLineSegment(sketch, "E205.direction1", {"start": v(-136.65, -45.72) * mm, "end": v(-129.03, -45.72) * mm, "construction": true});
            skLineSegment(sketch, "E205.direction2", {"start": v(-136.65, -45.72) * mm, "end": v(-136.65, -53.34) * mm, "construction": true});
            skLineSegment(sketch, "E206", {"start": v(-121.73, -19.05) * mm, "end": v(-143.95, -19.05) * mm, "construction": true});
            skLineSegment(sketch, "E207", {"start": v(-132.84, -45.72) * mm, "end": v(-132.84, -19.05) * mm, "construction": true});
            skLineSegment(sketch, "E208.MirrorCS", {"start": v(136.65, -45.72) * mm, "end": v(129.03, -45.72) * mm, "construction": true});
            skLineSegment(sketch, "E209.MirrorCS", {"start": v(136.65, -45.72) * mm, "end": v(136.65, -53.34) * mm, "construction": true});
            skCircle(sketch, "E210.MirrorC", {"center": v(136.65, -53.34) * mm, "radius": 1.98 * mm});
            skCircle(sketch, "E211.MirrorC", {"center": v(129.03, -45.72) * mm, "radius": 1.98 * mm});
            skCircle(sketch, "E212.MirrorC", {"center": v(129.03, -53.34) * mm, "radius": 1.98 * mm});
            skCircle(sketch, "E213.MirrorC", {"center": v(136.65, -45.72) * mm, "radius": 1.98 * mm});
            skSolve(sketch);
        }
        {
            var Q0;
            Q0=makeQuery(id+"F0.imprint","IMPRINT",FACE,{"disambiguationData":[TD([[makeQuery(id+"F0.imprint","IMPRINT",EDGE,{"derivedFrom":sQuery(id+"F0.wireOp",EDGE,"E0.MirrorCS")}),1.0]])]});
            extrude(context, id + "F1", {"entities" : qUnion([Q0]), "depth" : 3.17 * mm});
        }
    });
